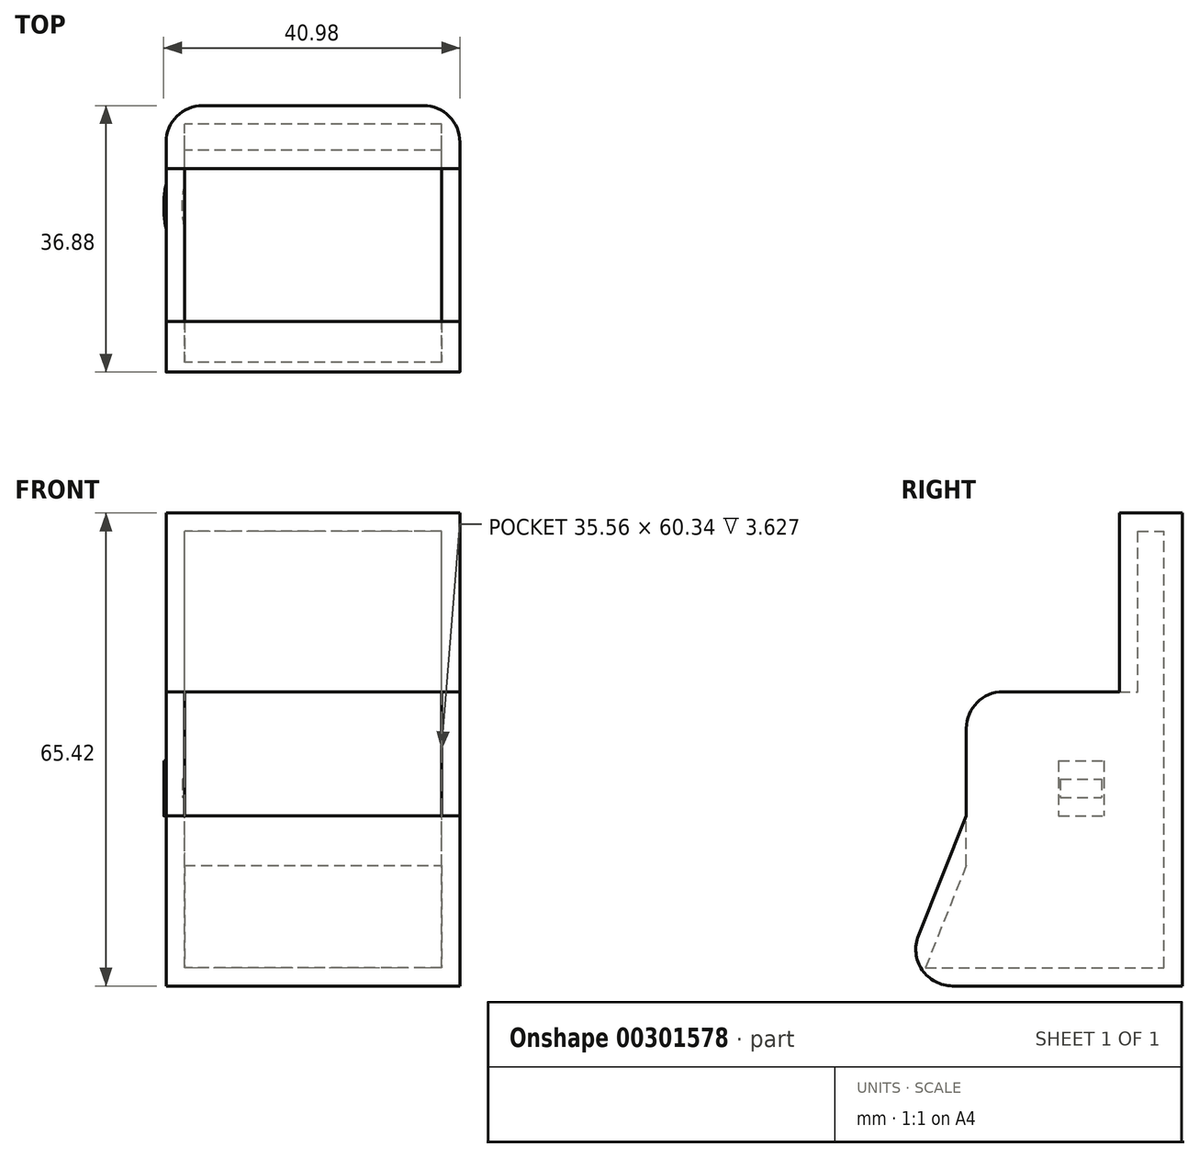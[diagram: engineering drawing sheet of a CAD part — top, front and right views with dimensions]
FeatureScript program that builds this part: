
annotation { "Feature Type Name" : "Feature", "Feature Type Description" : "" }
export const myFeature = defineFeature(function(context is Context, id is Id, definition is map)
    precondition{}
    {
        {
            var Q0;
            Q0=qCreatedBy(makeId("Top.planeOp"),FACE);
            var sketch = newSketch(context, id + "F0", { "sketchPlane" : qUnion([Q0])});
            skLineSegment(sketch, "E0", {"start": v(-12.5, 0) * mm, "end": v(12.9, 0) * mm});
            skFitSpline(sketch, "E1", {"points": [v(-12.5, 0) * mm, v(-17.88, 23.77) * mm, v(16.94, 24) * mm, v(12.9, 0) * mm, v(-12.5, 0) * mm]});
            skSolve(sketch);
        }
        {
            var Q0;
            Q0=makeQuery(id+"F0.imprint","IMPRINT",FACE,{"disambiguationData":[TD([[makeQuery(id+"F0.imprint","IMPRINT",EDGE,{"derivedFrom":sQuery(id+"F0.wireOp",EDGE,"E0")}),1.0]])]});
            extrude(context, id + "F1", {"entities" : qUnion([Q0]), "depth" : 7.62 * mm});
        }
        {
            var Q0;
            Q0=qCreatedBy(makeId("Right.planeOp"),FACE);
            var sketch = newSketch(context, id + "F2", { "sketchPlane" : qUnion([Q0])});
            skLineSegment(sketch, "E2", {"start": v(0, 0) * mm, "end": v(-9.41, -23.53) * mm});
            skLineSegment(sketch, "E3", {"start": v(-9.41, -23.53) * mm, "end": v(29.89, -23.53) * mm});
            skLineSegment(sketch, "E4", {"start": v(29.89, -23.53) * mm, "end": v(29.89, 41.89) * mm});
            skLineSegment(sketch, "E5", {"start": v(0, 0) * mm, "end": v(0, 17.18) * mm});
            skLineSegment(sketch, "E6", {"start": v(0, 17.18) * mm, "end": v(15.06, 17.18) * mm});
            skLineSegment(sketch, "E7", {"start": v(15.06, 17.18) * mm, "end": v(21.18, 17.18) * mm});
            skLineSegment(sketch, "E8", {"start": v(21.18, 17.18) * mm, "end": v(21.18, 41.89) * mm});
            skLineSegment(sketch, "E9", {"start": v(21.18, 41.89) * mm, "end": v(29.89, 41.89) * mm});
            skSolve(sketch);
        }
        {
            var Q0;
            Q0=makeQuery(id+"F2.imprint","IMPRINT",FACE,{"disambiguationData":[TD([[makeQuery(id+"F2.imprint","IMPRINT",EDGE,{"derivedFrom":sQuery(id+"F2.wireOp",EDGE,"E2")}),1.0]])]});
            extrude(context, id + "F3", {"entities" : qUnion([Q0]), "operationType" : NewBodyOperationType.ADD, "endBound" : BoundingType.SYMMETRIC, "depth" : 40.64 * mm});
        }
        {
            var Q0;
            Q0=makeQuery(id+"F3.boolean.opBoolean","MERGE",FACE,{"derivedFrom":[makeQuery(id+"F1.opExtrude","SWEPT_FACE",FACE,{"disambiguationData":[OSD([sQuery(id+"F0.wireOp",EDGE,"E0")])]}),makeQuery(id+"F3.opExtrude","SWEPT_FACE",FACE,{"disambiguationData":[OSD([sQuery(id+"F2.wireOp",EDGE,"E5")])]})]});
            var Q1;
            Q1=makeQuery(id+"F3.opExtrude","SWEPT_FACE",FACE,{"disambiguationData":[OSD([sQuery(id+"F2.wireOp",EDGE,"E6"),sQuery(id+"F2.wireOp",EDGE,"E7")])]});
            shell(context, id + "F4", {"entities" : qUnion([Q0, Q1]), "thickness" : 2.54 * mm});
        }
        {
            var Q0;
            Q0=makeQuery(id+"F3.opExtrude","SWEPT_EDGE",EDGE,{"disambiguationData":[OSD([sQuery(id+"F2.wireOp",EDGE,"E2"),sQuery(id+"F2.wireOp",EDGE,"E3")])]});
            fillet(context, id + "F5", {"entities" : qUnion([Q0]), "radius" : 5.08 * mm, "tangentPropagation" : true, "allowEdgeOverflow" : false});
        }
        {
            var Q0;
            Q0=makeQuery(id+"F3.opExtrude","CAP_EDGE",EDGE,{"disambiguationData":[OSD([sQuery(id+"F2.wireOp",EDGE,"E4")])],"isStart":true});
            var Q1;
            Q1=makeQuery(id+"F3.opExtrude","CAP_EDGE",EDGE,{"disambiguationData":[OSD([sQuery(id+"F2.wireOp",EDGE,"E4")])],"isStart":false});
            var Q2;
            Q2=makeQuery(id+"F4.opShell","OFFSET_EDGE",EDGE,{"disambiguationData":[OSD([sQuery(id+"F2.wireOp",EDGE,"E5"),sQuery(id+"F2.wireOp",EDGE,"E6")])]});
            var Q3;
            Q3=makeQuery(id+"F3.opExtrude","SWEPT_EDGE",EDGE,{"disambiguationData":[OSD([sQuery(id+"F2.wireOp",EDGE,"E5"),sQuery(id+"F2.wireOp",EDGE,"E6")])]});
            fillet(context, id + "F6", {"entities" : qUnion([Q0, Q1, Q2, Q3]), "radius" : 5.08 * mm, "tangentPropagation" : true, "allowEdgeOverflow" : false});
        }
    });
